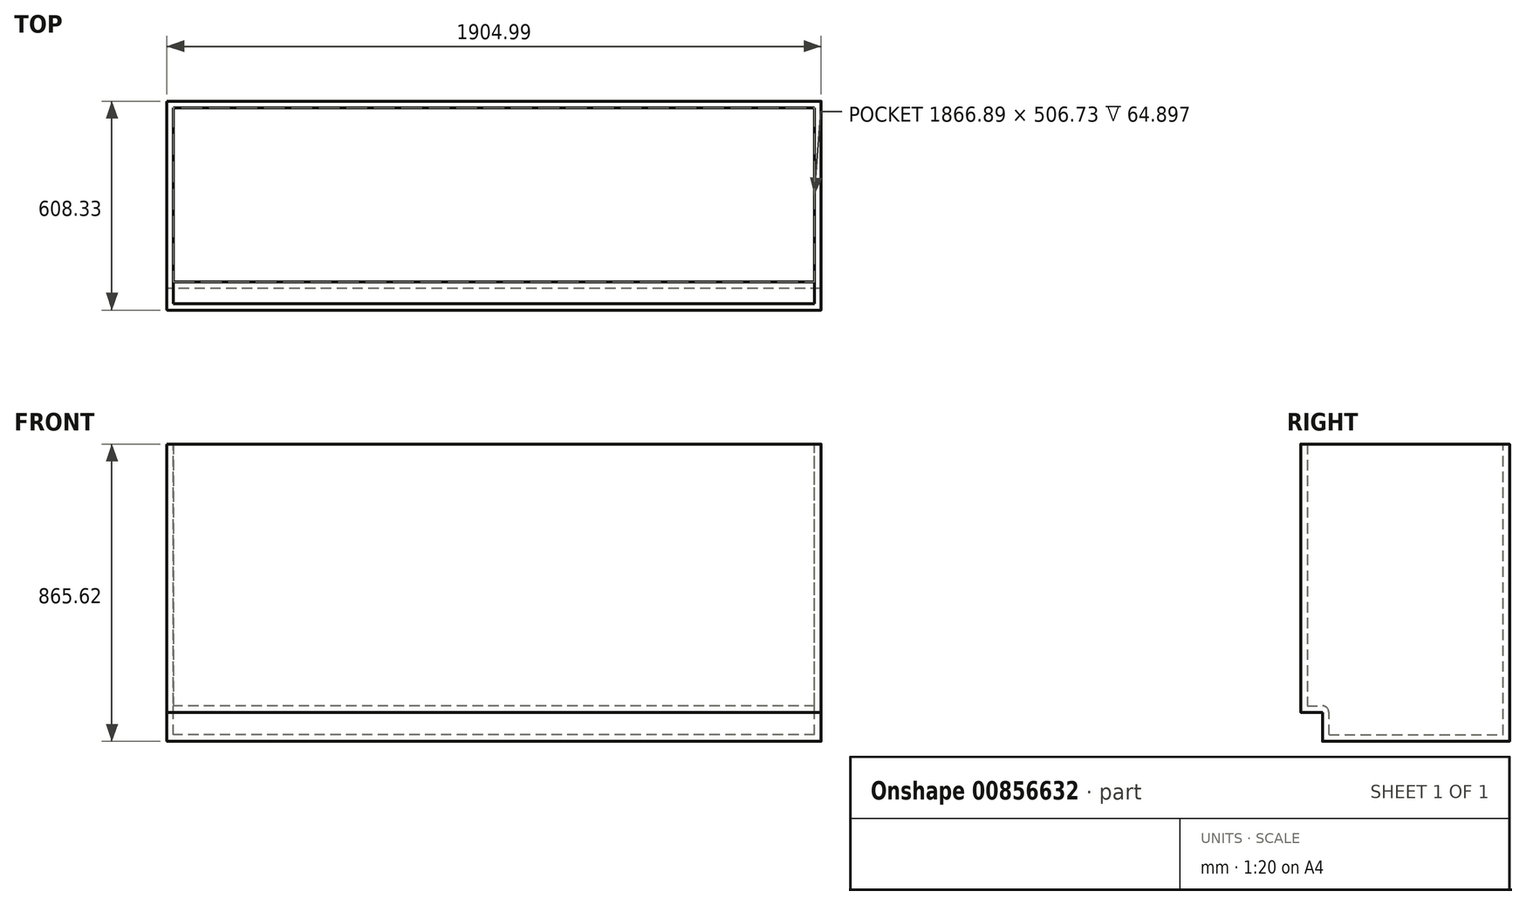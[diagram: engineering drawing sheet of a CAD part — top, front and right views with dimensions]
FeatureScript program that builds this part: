
annotation { "Feature Type Name" : "Feature", "Feature Type Description" : "" }
export const myFeature = defineFeature(function(context is Context, id is Id, definition is map)
    precondition{}
    {
        {
            var Q0;
            Q0=qCreatedBy(makeId("Front.planeOp"),FACE);
            var sketch = newSketch(context, id + "F0", { "sketchPlane" : qUnion([Q0])});
            skLineSegment(sketch, "E0.bottom", {"start": v(1208.67, 0) * mm, "end": v(2113.54, 0) * mm});
            skLineSegment(sketch, "E0.top", {"start": v(1208.67, 1778) * mm, "end": v(2113.54, 1778) * mm});
            skLineSegment(sketch, "E0.left", {"start": v(1208.67, 0) * mm, "end": v(1208.67, 1778) * mm});
            skLineSegment(sketch, "E0.right", {"start": v(2113.54, 0) * mm, "end": v(2113.54, 1778) * mm});
            skLineSegment(sketch, "E1.left", {"start": v(0, 0) * mm, "end": v(0.1, 863.6) * mm});
            skLineSegment(sketch, "E2.top", {"start": v(0.1, 901.7) * mm, "end": v(-2504.34, 901.7) * mm});
            skLineSegment(sketch, "E2.left", {"start": v(0.1, 863.6) * mm, "end": v(0.1, 901.7) * mm});
            skLineSegment(sketch, "E2.right", {"start": v(-2504.34, 863.6) * mm, "end": v(-2504.34, 901.7) * mm});
            skLineSegment(sketch, "E3.bottom", {"start": v(0, 0) * mm, "end": v(-381, 0) * mm});
            skLineSegment(sketch, "E3.left", {"start": v(0, 0) * mm, "end": v(0, 863.47) * mm});
            skLineSegment(sketch, "E4", {"start": v(-381, 0) * mm, "end": v(-387.35, 0) * mm, "construction": true});
            skLineSegment(sketch, "E5.bottom", {"start": v(-387.35, 857.25) * mm, "end": v(-1143, 857.25) * mm, "construction": true});
            skLineSegment(sketch, "E6.bottom", {"start": v(-1149.35, 857.25) * mm, "end": v(-1527.18, 857.25) * mm});
            skLineSegment(sketch, "E7.bottom", {"start": v(0, 863.47) * mm, "end": v(-381, 857.25) * mm});
            skLineSegment(sketch, "E7.left", {"start": v(0, 863.47) * mm, "end": v(0, 82.55) * mm});
            skLineSegment(sketch, "E8.bottom", {"start": v(-1904.99, -2.15) * mm, "end": v(0, -2.15) * mm});
            skLineSegment(sketch, "E8.top", {"start": v(-1904.99, 863.47) * mm, "end": v(0, 863.47) * mm});
            skLineSegment(sketch, "E8.left", {"start": v(-1904.99, -2.15) * mm, "end": v(-1904.99, 863.47) * mm});
            skLineSegment(sketch, "E8.right", {"start": v(0, -2.15) * mm, "end": v(0, 863.47) * mm});
            skSolve(sketch);
        }
        {
            var Q0;
            {var subQ2=sQuery(id+"F0.wireOp",EDGE,"E8.bottom");Q0=makeQuery(id+"F0.imprint","IMPRINT",FACE,{"disambiguationData":[TD([[makeQuery(id+"F0.imprint","IMPRINT",EDGE,{"derivedFrom":subQ2}),1.0]])]});}
            extrude(context, id + "F1", {"entities" : qUnion([Q0]), "oppositeDirection" : true, "depth" : 609.6 * mm, "offsetDistance" : 25.4 * mm, "hasSecondDirection" : true, "secondDirectionOppositeDirection" : true, "secondDirectionDepth" : 1.27 * mm});
        }
        {
            var Q0;
            Q0=makeQuery(id+"F1.opExtrude","SWEPT_FACE",FACE,{"disambiguationData":[OSD([sQuery(id+"F0.wireOp",EDGE,"E8.left")])]});
            var sketch = newSketch(context, id + "F2", { "sketchPlane" : qUnion([Q0])});
            skLineSegment(sketch, "E9.bottom", {"start": v(-1.27, -2.15) * mm, "end": v(-64.77, -2.15) * mm});
            skLineSegment(sketch, "E9.top", {"start": v(-1.27, 82.43) * mm, "end": v(-64.77, 82.43) * mm});
            skLineSegment(sketch, "E9.left", {"start": v(-1.27, -2.15) * mm, "end": v(-1.27, 82.43) * mm});
            skLineSegment(sketch, "E9.right", {"start": v(-64.77, -2.15) * mm, "end": v(-64.77, 82.43) * mm});
            skSolve(sketch);
        }
        {
            var Q0;
            Q0 = qSketchRegion(id + "F2", true);
            extrude(context, id + "F3", {"entities" : qUnion([Q0]), "operationType" : NewBodyOperationType.REMOVE, "endBound" : BoundingType.UP_TO_NEXT, "oppositeDirection" : true, "depth" : 25.4 * mm, "offsetDistance" : 25.4 * mm});
        }
        {
            var Q0;
            Q0=makeQuery(id+"F3.boolean.opBoolean","COPY",EDGE,{"derivedFrom":makeQuery(id+"F3.opExtrude","CAP_EDGE",EDGE,{"disambiguationData":[OSD([sQuery(id+"F2.wireOp",EDGE,"E9.top")])],"isStart":true})});
            var Q1;
            Q1=makeQuery(id+"F3.boolean.opBoolean","COPY",EDGE,{"derivedFrom":makeQuery(id+"F3.opExtrude","CAP_EDGE",EDGE,{"disambiguationData":[OSD([sQuery(id+"F2.wireOp",EDGE,"E9.right")])],"isStart":true})});
            var Q2;
            Q2=makeQuery(id+"F1.opExtrude","CAP_EDGE",EDGE,{"disambiguationData":[OSD([sQuery(id+"F0.wireOp",EDGE,"E8.left")])],"isStart":true});
            var Q3;
            Q3=makeQuery(id+"F3.boolean.opBoolean","COPY",EDGE,{"derivedFrom":makeQuery(id+"F3.opExtrude","SWEPT_EDGE",EDGE,{"disambiguationData":[OSD([sQuery(id+"F0.wireOp",EDGE,"E8.left"),sQuery(id+"F2.wireOp",EDGE,"E9.top"),sQuery(id+"F2.wireOp",EDGE,"E9.left")])]})});
            var Q4;
            Q4=makeQuery(id+"F1.opExtrude","CAP_EDGE",EDGE,{"disambiguationData":[OSD([sQuery(id+"F0.wireOp",EDGE,"E8.right")])],"isStart":true});
            var Q5;
            Q5=makeQuery(id+"F3.boolean.opBoolean","COPY",EDGE,{"derivedFrom":makeQuery(id+"F3.opExtrude","CAP_EDGE",EDGE,{"disambiguationData":[OSD([sQuery(id+"F2.wireOp",EDGE,"E9.top")])],"isStart":false})});
            var Q6;
            Q6=makeQuery(id+"F3.boolean.opBoolean","COPY",EDGE,{"derivedFrom":makeQuery(id+"F3.opExtrude","CAP_EDGE",EDGE,{"disambiguationData":[OSD([sQuery(id+"F2.wireOp",EDGE,"E9.right")])],"isStart":false})});
            var Q7;
            Q7=makeQuery(id+"F3.boolean.opBoolean","COPY",EDGE,{"derivedFrom":makeQuery(id+"F3.opExtrude","SWEPT_EDGE",EDGE,{"disambiguationData":[OSD([sQuery(id+"F0.wireOp",EDGE,"E8.bottom"),sQuery(id+"F0.wireOp",EDGE,"E8.left"),sQuery(id+"F2.wireOp",EDGE,"E9.bottom"),sQuery(id+"F2.wireOp",EDGE,"E9.right")])]})});
            var Q8;
            Q8=makeQuery(id+"F3.boolean.opBoolean","COPY",EDGE,{"derivedFrom":makeQuery(id+"F3.opExtrude","SWEPT_EDGE",EDGE,{"disambiguationData":[OSD([sQuery(id+"F2.wireOp",EDGE,"E9.top"),sQuery(id+"F2.wireOp",EDGE,"E9.right")])]})});
            var Q9;
            Q9=makeQuery(id+"F1.opExtrude","SWEPT_FACE",FACE,{"disambiguationData":[OSD([sQuery(id+"F0.wireOp",EDGE,"E8.right")])]});
            var Q10;
            Q10=makeQuery(id+"F1.opExtrude","SWEPT_EDGE",EDGE,{"disambiguationData":[OSD([sQuery(id+"F0.wireOp",EDGE,"E8.bottom"),sQuery(id+"F0.wireOp",EDGE,"E8.right")])]});
            var Q11;
            Q11=makeQuery(id+"F1.opExtrude","SWEPT_EDGE",EDGE,{"disambiguationData":[OSD([sQuery(id+"F0.wireOp",EDGE,"E8.bottom"),sQuery(id+"F0.wireOp",EDGE,"E8.left")])]});
            fillet(context, id + "F4", {"entities" : qUnion([Q0, Q1, Q2, Q3, Q4, Q5, Q6, Q7, Q8, Q9, Q10, Q11]), "radius" : 0.64 * mm, "tangentPropagation" : true, "allowEdgeOverflow" : false});
        }
        {
            var Q0;
            Q0=makeQuery(id+"F1.opExtrude","SWEPT_FACE",FACE,{"disambiguationData":[OSD([sQuery(id+"F0.wireOp",EDGE,"E8.top")])]});
            shell(context, id + "F5", {"entities" : qUnion([Q0]), "thickness" : 19.05 * mm});
        }
    });
